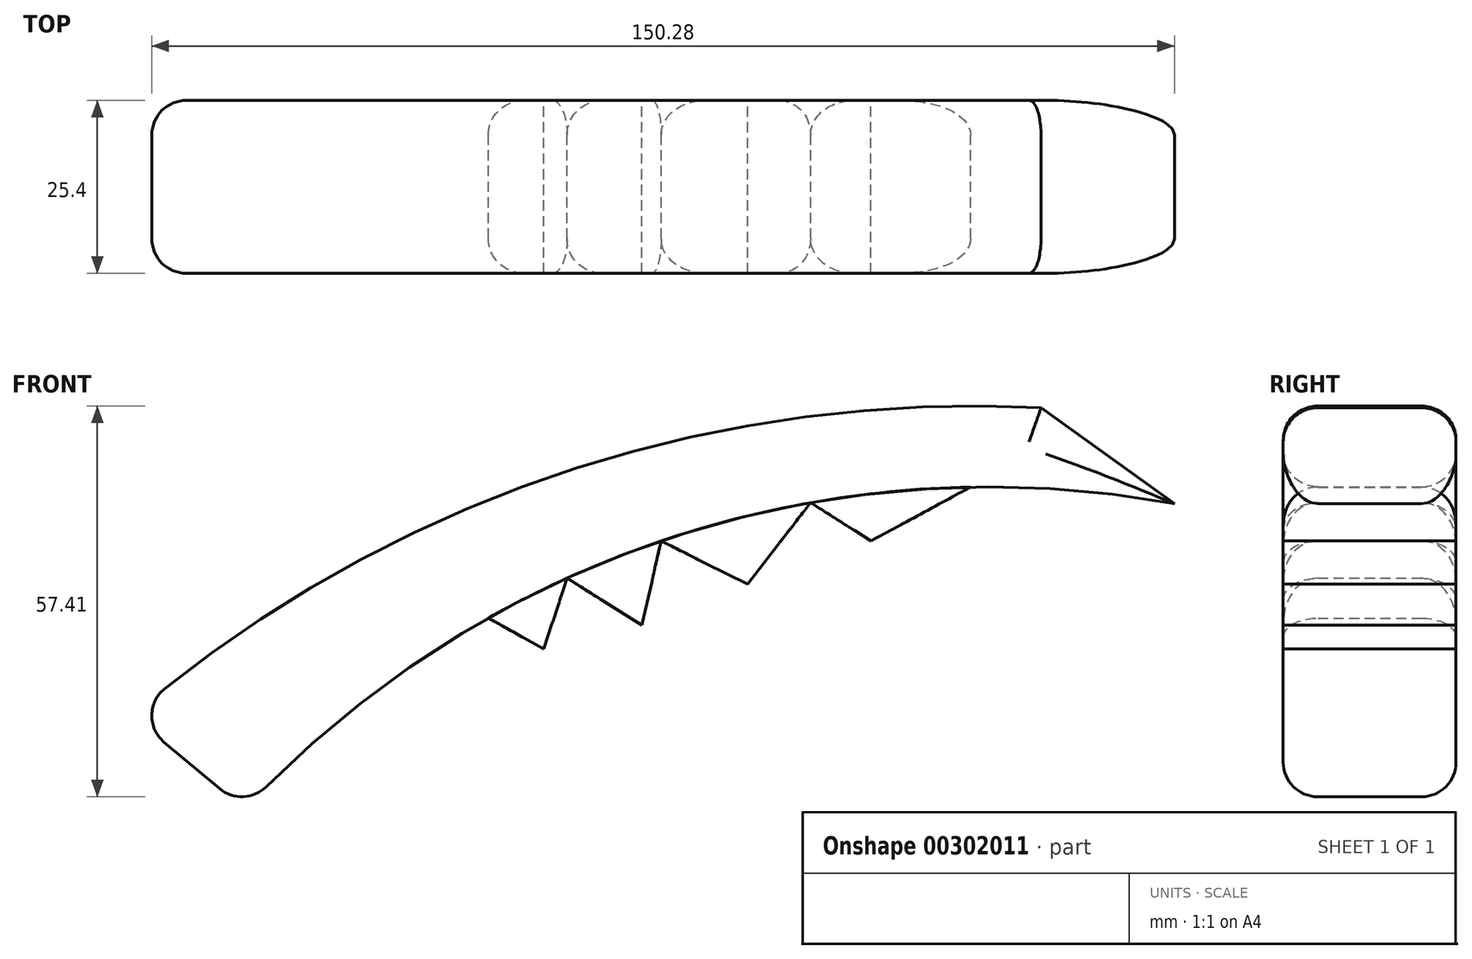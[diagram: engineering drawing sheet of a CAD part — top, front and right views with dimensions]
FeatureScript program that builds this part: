
annotation { "Feature Type Name" : "Feature", "Feature Type Description" : "" }
export const myFeature = defineFeature(function(context is Context, id is Id, definition is map)
    precondition{}
    {
        {
            var Q0;
            Q0=qCreatedBy(makeId("Front.planeOp"),FACE);
            var sketch = newSketch(context, id + "F0", { "sketchPlane" : qUnion([Q0])});
            skArc(sketch, "E0", {"start": v(69.65, 0) * mm, "mid": v(-1.46, -9.79) * mm, "end": v(-63.9, -45.19) * mm});
            skLineSegment(sketch, "E1", {"start": v(-63.9, -45.19) * mm, "end": v(-47.45, -59) * mm});
            skArc(sketch, "E2", {"start": v(89.25, -14.1) * mm, "mid": v(15.18, -19.12) * mm, "end": v(-47.45, -59) * mm});
            skLineSegment(sketch, "E3", {"start": v(69.65, 0) * mm, "end": v(89.25, -14.1) * mm});
            skLineSegment(sketch, "E4", {"start": v(59.3, -11.65) * mm, "end": v(44.64, -19.57) * mm});
            skLineSegment(sketch, "E5", {"start": v(44.64, -19.57) * mm, "end": v(35.8, -13.93) * mm});
            skLineSegment(sketch, "E6", {"start": v(35.8, -13.93) * mm, "end": v(26.51, -25.9) * mm});
            skLineSegment(sketch, "E7", {"start": v(26.51, -25.9) * mm, "end": v(13.83, -19.57) * mm});
            skLineSegment(sketch, "E8", {"start": v(13.83, -19.57) * mm, "end": v(10.97, -31.95) * mm});
            skLineSegment(sketch, "E9", {"start": v(10.97, -31.95) * mm, "end": v(0, -25.03) * mm});
            skLineSegment(sketch, "E10", {"start": v(0, -25.03) * mm, "end": v(-3.42, -35.4) * mm});
            skLineSegment(sketch, "E11", {"start": v(-3.42, -35.4) * mm, "end": v(-11.58, -30.9) * mm});
            skSolve(sketch);
        }
        {
            var Q0;
            Q0=makeQuery(id+"F0.imprint","IMPRINT",FACE,{"disambiguationData":[TD([[makeQuery(id+"F0.imprint","IMPRINT",EDGE,{"derivedFrom":sQuery(id+"F0.wireOp",EDGE,"E0")}),1.0]])]});
            extrude(context, id + "F1", {"entities" : qUnion([Q0]), "depth" : 25.4 * mm});
        }
        {
            var Q0;
            {var subQ0=sQuery(id+"F0.wireOp",EDGE,"E10");Q0=makeQuery(id+"F0.imprint","IMPRINT",FACE,{"disambiguationData":[TD([[makeQuery(id+"F0.imprint","IMPRINT",EDGE,{"derivedFrom":subQ0}),-1.0]])]});}
            var Q1;
            {var subQ0=sQuery(id+"F0.wireOp",EDGE,"E8");Q1=makeQuery(id+"F0.imprint","IMPRINT",FACE,{"disambiguationData":[TD([[makeQuery(id+"F0.imprint","IMPRINT",EDGE,{"derivedFrom":subQ0}),-1.0]])]});}
            var Q2;
            {var subQ0=sQuery(id+"F0.wireOp",EDGE,"E6");Q2=makeQuery(id+"F0.imprint","IMPRINT",FACE,{"disambiguationData":[TD([[makeQuery(id+"F0.imprint","IMPRINT",EDGE,{"derivedFrom":subQ0}),-1.0]])]});}
            var Q3;
            {var subQ0=sQuery(id+"F0.wireOp",EDGE,"E4");Q3=makeQuery(id+"F0.imprint","IMPRINT",FACE,{"disambiguationData":[TD([[makeQuery(id+"F0.imprint","IMPRINT",EDGE,{"derivedFrom":subQ0}),-1.0]])]});}
            extrude(context, id + "F2", {"entities" : qUnion([Q0, Q1, Q2, Q3]), "depth" : 25.4 * mm});
        }
        {
            var Q0;
            Q0=makeQuery(id+"F1.opExtrude","CAP_EDGE",EDGE,{"disambiguationData":[OSD([sQuery(id+"F0.wireOp",EDGE,"E0")])],"isStart":false});
            var Q1;
            Q1=makeQuery(id+"F1.opExtrude","CAP_EDGE",EDGE,{"disambiguationData":[OSD([sQuery(id+"F0.wireOp",EDGE,"E1")])],"isStart":false});
            var Q2;
            Q2=makeQuery(id+"F1.opExtrude","CAP_EDGE",EDGE,{"disambiguationData":[OSD([sQuery(id+"F0.wireOp",EDGE,"E3")])],"isStart":false});
            var Q3;
            Q3=makeQuery(id+"F1.opExtrude","CAP_EDGE",EDGE,{"disambiguationData":[OSD([sQuery(id+"F0.wireOp",EDGE,"E2")])],"isStart":false});
            var Q4;
            Q4=makeQuery(id+"F1.opExtrude","SWEPT_EDGE",EDGE,{"disambiguationData":[OSD([sQuery(id+"F0.wireOp",EDGE,"E0"),sQuery(id+"F0.wireOp",EDGE,"E1")])]});
            var Q5;
            Q5=makeQuery(id+"F1.opExtrude","SWEPT_EDGE",EDGE,{"disambiguationData":[OSD([sQuery(id+"F0.wireOp",EDGE,"E1"),sQuery(id+"F0.wireOp",EDGE,"E2")])]});
            var Q6;
            Q6=makeQuery(id+"F1.opExtrude","CAP_EDGE",EDGE,{"disambiguationData":[OSD([sQuery(id+"F0.wireOp",EDGE,"E1")])],"isStart":true});
            var Q7;
            Q7=makeQuery(id+"F1.opExtrude","CAP_EDGE",EDGE,{"disambiguationData":[OSD([sQuery(id+"F0.wireOp",EDGE,"E0")])],"isStart":true});
            var Q8;
            Q8=makeQuery(id+"F1.opExtrude","CAP_EDGE",EDGE,{"disambiguationData":[OSD([sQuery(id+"F0.wireOp",EDGE,"E2")])],"isStart":true});
            var Q9;
            Q9=makeQuery(id+"F1.opExtrude","CAP_EDGE",EDGE,{"disambiguationData":[OSD([sQuery(id+"F0.wireOp",EDGE,"E3")])],"isStart":true});
            fillet(context, id + "F3", {"entities" : qUnion([Q0, Q1, Q2, Q3, Q4, Q5, Q6, Q7, Q8, Q9]), "radius" : 5.08 * mm, "tangentPropagation" : true, "allowEdgeOverflow" : false});
        }
        {
            var Q0;
            {var subQ0=sQuery(id+"F0.wireOp",EDGE,"E2");Q0=makeQuery(id+"F2.opExtrude","CAP_EDGE",EDGE,{"disambiguationData":[OSD([subQ0]),TDD([makeQuery(id+"F0.imprint","IMPRINT",EDGE,{"disambiguationData":[TD([[makeQuery(id+"F0.imprint","INTERSECT",VERTEX,{"derivedFrom":[subQ0,sQuery(id+"F0.wireOp",EDGE,"E11")]}),1.0]])],"derivedFrom":subQ0})])],"isStart":false});}
            var Q1;
            {var subQ0=sQuery(id+"F0.wireOp",EDGE,"E2");Q1=makeQuery(id+"F2.opExtrude","CAP_EDGE",EDGE,{"disambiguationData":[OSD([subQ0]),TDD([makeQuery(id+"F0.imprint","IMPRINT",EDGE,{"disambiguationData":[TD([[makeQuery(id+"F0.imprint","INTERSECT",VERTEX,{"derivedFrom":[subQ0,sQuery(id+"F0.wireOp",EDGE,"E7"),sQuery(id+"F0.wireOp",EDGE,"E8")]}),-1.0]])],"derivedFrom":subQ0})])],"isStart":false});}
            var Q2;
            {var subQ0=sQuery(id+"F0.wireOp",EDGE,"E2");Q2=makeQuery(id+"F2.opExtrude","CAP_EDGE",EDGE,{"disambiguationData":[OSD([subQ0]),TDD([makeQuery(id+"F0.imprint","IMPRINT",EDGE,{"disambiguationData":[TD([[makeQuery(id+"F0.imprint","INTERSECT",VERTEX,{"derivedFrom":[subQ0,sQuery(id+"F0.wireOp",EDGE,"E5"),sQuery(id+"F0.wireOp",EDGE,"E6")]}),-1.0]])],"derivedFrom":subQ0})])],"isStart":false});}
            var Q3;
            {var subQ0=sQuery(id+"F0.wireOp",EDGE,"E2");Q3=makeQuery(id+"F2.opExtrude","CAP_EDGE",EDGE,{"disambiguationData":[OSD([subQ0]),TDD([makeQuery(id+"F0.imprint","IMPRINT",EDGE,{"disambiguationData":[TD([[makeQuery(id+"F0.imprint","INTERSECT",VERTEX,{"derivedFrom":[subQ0,sQuery(id+"F0.wireOp",EDGE,"E4")]}),-1.0]])],"derivedFrom":subQ0})])],"isStart":false});}
            var Q4;
            {var subQ0=sQuery(id+"F0.wireOp",EDGE,"E2");Q4=makeQuery(id+"F2.opExtrude","CAP_EDGE",EDGE,{"disambiguationData":[OSD([subQ0]),TDD([makeQuery(id+"F0.imprint","IMPRINT",EDGE,{"disambiguationData":[TD([[makeQuery(id+"F0.imprint","INTERSECT",VERTEX,{"derivedFrom":[subQ0,sQuery(id+"F0.wireOp",EDGE,"E11")]}),1.0]])],"derivedFrom":subQ0})])],"isStart":true});}
            var Q5;
            {var subQ0=sQuery(id+"F0.wireOp",EDGE,"E2");Q5=makeQuery(id+"F2.opExtrude","CAP_EDGE",EDGE,{"disambiguationData":[OSD([subQ0]),TDD([makeQuery(id+"F0.imprint","IMPRINT",EDGE,{"disambiguationData":[TD([[makeQuery(id+"F0.imprint","INTERSECT",VERTEX,{"derivedFrom":[subQ0,sQuery(id+"F0.wireOp",EDGE,"E7"),sQuery(id+"F0.wireOp",EDGE,"E8")]}),-1.0]])],"derivedFrom":subQ0})])],"isStart":true});}
            var Q6;
            {var subQ0=sQuery(id+"F0.wireOp",EDGE,"E2");Q6=makeQuery(id+"F2.opExtrude","CAP_EDGE",EDGE,{"disambiguationData":[OSD([subQ0]),TDD([makeQuery(id+"F0.imprint","IMPRINT",EDGE,{"disambiguationData":[TD([[makeQuery(id+"F0.imprint","INTERSECT",VERTEX,{"derivedFrom":[subQ0,sQuery(id+"F0.wireOp",EDGE,"E5"),sQuery(id+"F0.wireOp",EDGE,"E6")]}),-1.0]])],"derivedFrom":subQ0})])],"isStart":true});}
            var Q7;
            {var subQ0=sQuery(id+"F0.wireOp",EDGE,"E2");Q7=makeQuery(id+"F2.opExtrude","CAP_EDGE",EDGE,{"disambiguationData":[OSD([subQ0]),TDD([makeQuery(id+"F0.imprint","IMPRINT",EDGE,{"disambiguationData":[TD([[makeQuery(id+"F0.imprint","INTERSECT",VERTEX,{"derivedFrom":[subQ0,sQuery(id+"F0.wireOp",EDGE,"E4")]}),-1.0]])],"derivedFrom":subQ0})])],"isStart":true});}
            fillet(context, id + "F4", {"entities" : qUnion([Q0, Q1, Q2, Q3, Q4, Q5, Q6, Q7]), "radius" : 5.08 * mm, "tangentPropagation" : true, "allowEdgeOverflow" : false});
        }
    });
